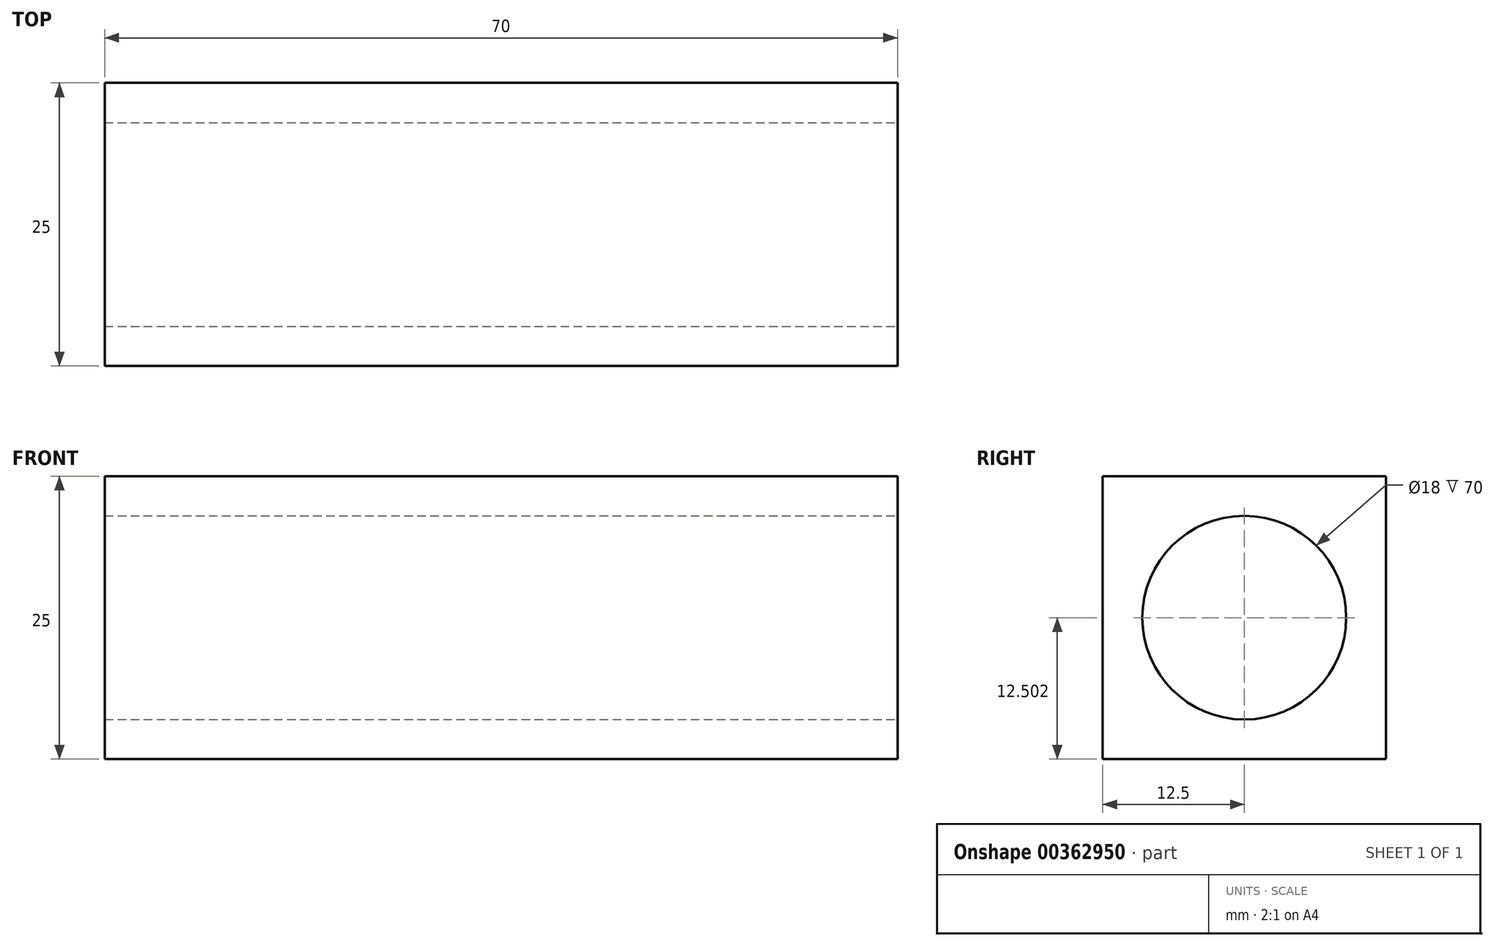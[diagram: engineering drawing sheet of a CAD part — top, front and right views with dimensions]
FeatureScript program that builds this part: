
annotation { "Feature Type Name" : "Feature", "Feature Type Description" : "" }
export const myFeature = defineFeature(function(context is Context, id is Id, definition is map)
    precondition{}
    {
        {
            var Q0;
            Q0=qCreatedBy(makeId("Front.planeOp"),FACE);
            var sketch = newSketch(context, id + "F0", { "sketchPlane" : qUnion([Q0])});
            skLineSegment(sketch, "E0.bottom", {"start": v(-71.93, 29.9) * mm, "end": v(-1.93, 29.9) * mm});
            skLineSegment(sketch, "E0.top", {"start": v(-71.93, 4.9) * mm, "end": v(-1.93, 4.9) * mm});
            skLineSegment(sketch, "E0.left", {"start": v(-71.93, 29.9) * mm, "end": v(-71.93, 4.9) * mm});
            skLineSegment(sketch, "E0.right", {"start": v(-1.93, 29.9) * mm, "end": v(-1.93, 4.9) * mm});
            skSolve(sketch);
        }
        {
            var Q0;
            Q0=makeQuery(id+"F0.imprint","IMPRINT",FACE,{"disambiguationData":[TD([[makeQuery(id+"F0.imprint","IMPRINT",EDGE,{"derivedFrom":sQuery(id+"F0.wireOp",EDGE,"E0.bottom")}),-1.0]])]});
            extrude(context, id + "F1", {"entities" : qUnion([Q0]), "depth" : 25 * mm});
        }
        {
            var Q0;
            Q0=makeQuery(id+"F1.opExtrude","SWEPT_FACE",FACE,{"disambiguationData":[OSD([sQuery(id+"F0.wireOp",EDGE,"E0.right")])]});
            var sketch = newSketch(context, id + "F2", { "sketchPlane" : qUnion([Q0])});
            skLineSegment(sketch, "E1", {"start": v(-12.5, 29.9) * mm, "end": v(-12.5, 4.9) * mm});
            skLineSegment(sketch, "E2", {"start": v(0, 17.4) * mm, "end": v(-25, 17.4) * mm});
            skCircle(sketch, "E3", {"center": v(-12.5, 17.4) * mm, "radius": 8.52 * mm});
            skSolve(sketch);
        }
        {
            var Q0;
            Q0=sQuery(id+"F2.wireOp",VERTEX,"E3.center");
            var Q1;
            Q1=makeQuery(id+"F1.opExtrude","SWEPT_BODY",BODY,{"disambiguationData":[OSD([sQuery(id+"F0.wireOp",EDGE,"E0.bottom"),sQuery(id+"F0.wireOp",EDGE,"E0.top"),sQuery(id+"F0.wireOp",EDGE,"E0.left"),sQuery(id+"F0.wireOp",EDGE,"E0.right")])]});
            hole(context, id + "F3", {"style" : HoleStyle.SIMPLE, "endStyle" : HoleEndStyle.THROUGH, "holeDiameter" : 18 * mm, "isTappedThrough" : true, "tappedDepth" : 12 * mm, "tapClearance" : 3, "startFromSketch" : true, "locations" : qUnion([Q0]), "scope" : qUnion([Q1])});
        }
    });
